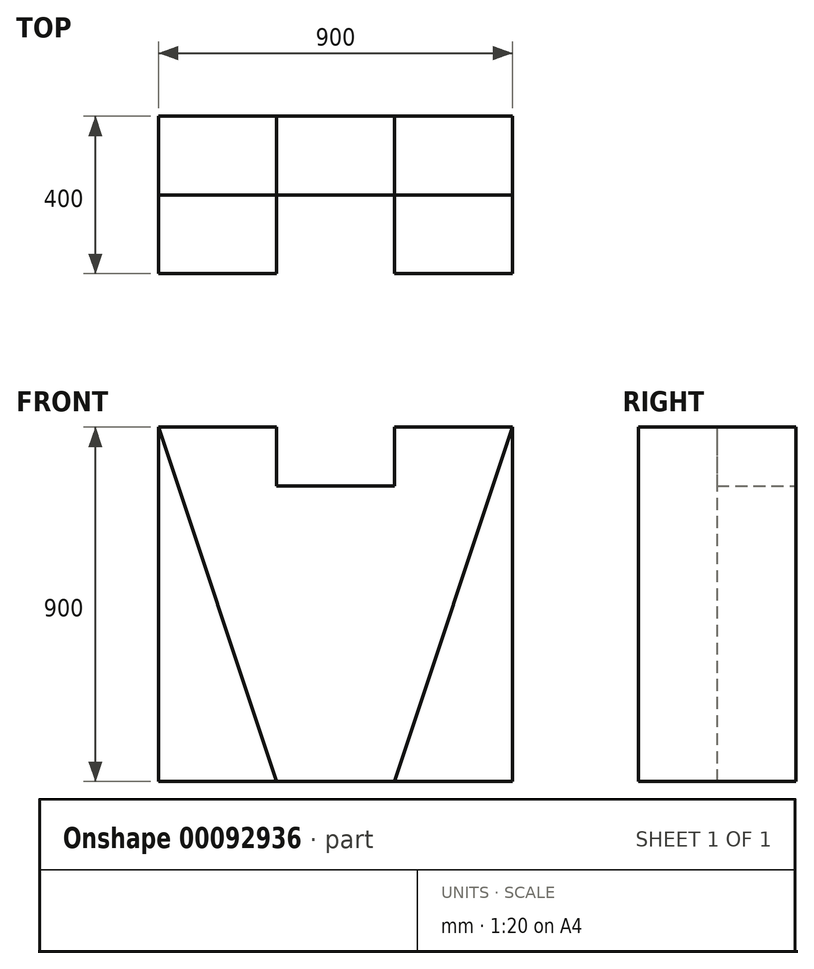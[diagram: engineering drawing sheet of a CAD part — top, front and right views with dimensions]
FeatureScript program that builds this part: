
annotation { "Feature Type Name" : "Feature", "Feature Type Description" : "" }
export const myFeature = defineFeature(function(context is Context, id is Id, definition is map)
    precondition{}
    {
        {
            var Q0;
            Q0=qCreatedBy(makeId("Front.planeOp"),FACE);
            var sketch = newSketch(context, id + "F0", { "sketchPlane" : qUnion([Q0])});
            skLineSegment(sketch, "E0.bottom", {"start": v(-450, 450) * mm, "end": v(-150, 450) * mm});
            skLineSegment(sketch, "E0.top", {"start": v(-450, -450) * mm, "end": v(450, -450) * mm});
            skLineSegment(sketch, "E0.left", {"start": v(-450, 450) * mm, "end": v(-450, -450) * mm});
            skLineSegment(sketch, "E0.right", {"start": v(450, 450) * mm, "end": v(450, -450) * mm});
            skPoint(sketch, "E0.middle", {"position": v(0, 0) * mm});
            skLineSegment(sketch, "E1.bottom", {"start": v(150, 300) * mm, "end": v(-150, 300) * mm});
            skLineSegment(sketch, "E1.left", {"start": v(150, 300) * mm, "end": v(150, 450) * mm});
            skLineSegment(sketch, "E1.right", {"start": v(-150, 300) * mm, "end": v(-150, 450) * mm});
            skPoint(sketch, "E1.middle", {"position": v(0, 450) * mm});
            skLineSegment(sketch, "E2.trimOffspring", {"start": v(150, 450) * mm, "end": v(450, 450) * mm});
            skSolve(sketch);
        }
        {
            var Q0;
            Q0 = qSketchRegion(id + "F0", true);
            extrude(context, id + "F1", {"entities" : qUnion([Q0]), "depth" : 200 * mm});
        }
        {
            var Q0;
            Q0=makeQuery(id+"F1.opExtrude","CAP_FACE",FACE,{"disambiguationData":[OSD([sQuery(id+"F0.wireOp",EDGE,"E0.bottom"),sQuery(id+"F0.wireOp",EDGE,"E0.top"),sQuery(id+"F0.wireOp",EDGE,"E0.left"),sQuery(id+"F0.wireOp",EDGE,"E0.right"),sQuery(id+"F0.wireOp",EDGE,"E1.bottom"),sQuery(id+"F0.wireOp",EDGE,"E1.left"),sQuery(id+"F0.wireOp",EDGE,"E1.right"),sQuery(id+"F0.wireOp",EDGE,"E2.trimOffspring")])],"isStart":false});
            var sketch = newSketch(context, id + "F2", { "sketchPlane" : qUnion([Q0])});
            skLineSegment(sketch, "E3", {"start": v(-450, -450) * mm, "end": v(-150, -450) * mm});
            skLineSegment(sketch, "E4", {"start": v(450, -450) * mm, "end": v(150, -450) * mm});
            skLineSegment(sketch, "E5", {"start": v(150, -450) * mm, "end": v(450, 450) * mm});
            skLineSegment(sketch, "E6", {"start": v(-150, -450) * mm, "end": v(-450, 450) * mm});
            skSolve(sketch);
        }
        {
            var Q0;
            Q0=makeQuery(id+"F2.imprint","IMPRINT",FACE,{"disambiguationData":[TD([[makeQuery(id+"F2.imprint","IMPRINT",EDGE,{"derivedFrom":sQuery(id+"F2.wireOp",EDGE,"E3")}),1.0]])]});
            var Q1;
            Q1=makeQuery(id+"F2.imprint","IMPRINT",FACE,{"disambiguationData":[TD([[makeQuery(id+"F2.imprint","IMPRINT",EDGE,{"derivedFrom":sQuery(id+"F2.wireOp",EDGE,"E4")}),1.0]])]});
            extrude(context, id + "F3", {"entities" : qUnion([Q0, Q1]), "operationType" : NewBodyOperationType.ADD, "depth" : 200 * mm});
        }
    });
